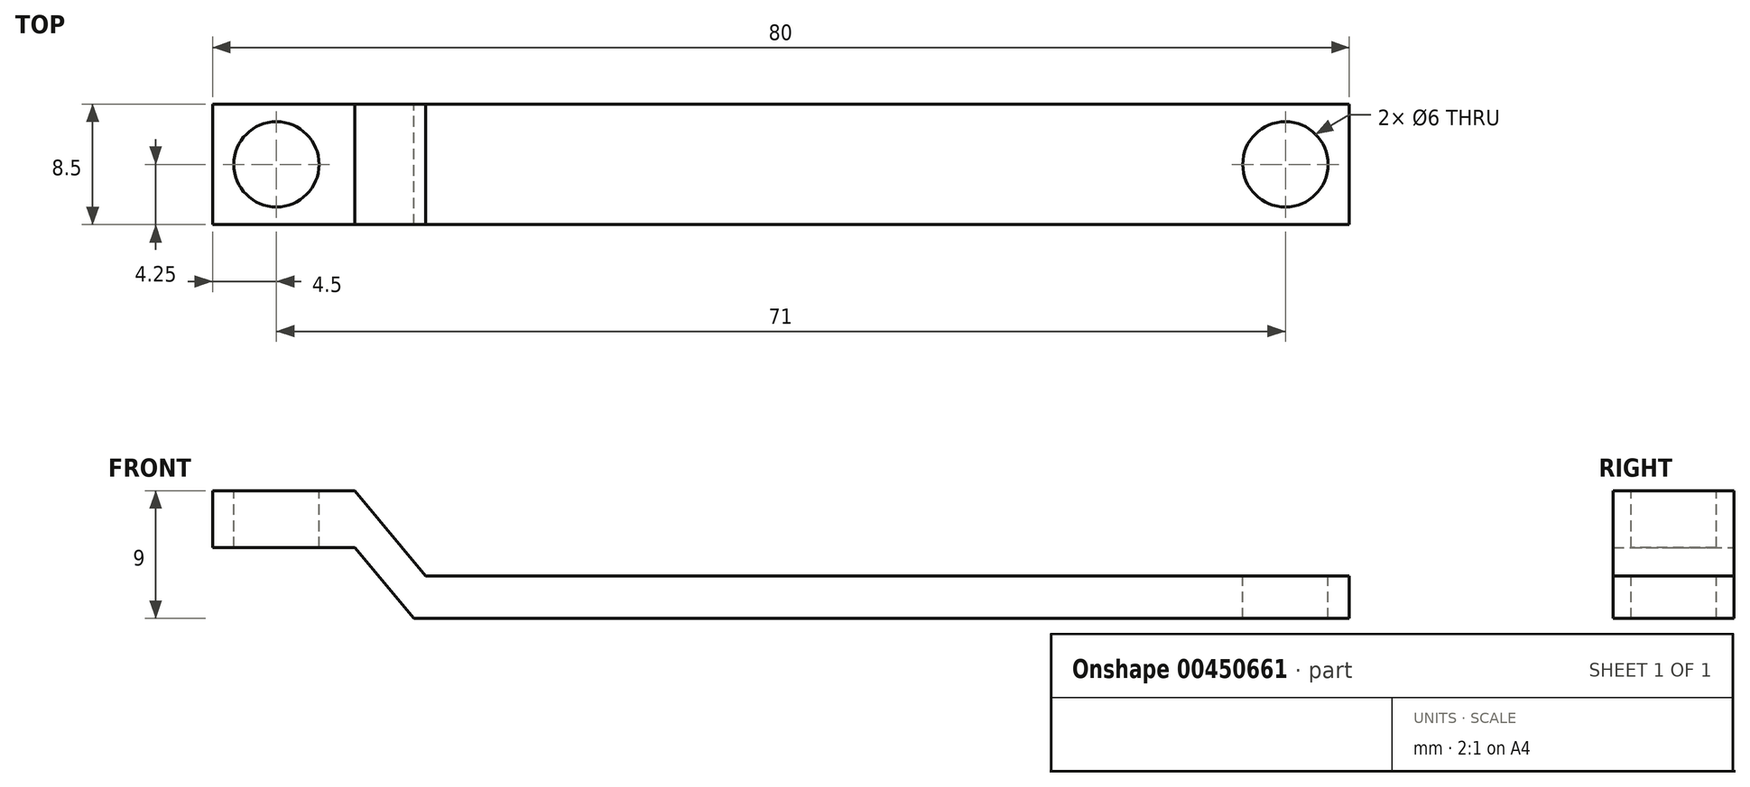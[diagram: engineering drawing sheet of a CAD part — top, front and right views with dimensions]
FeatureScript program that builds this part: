
annotation { "Feature Type Name" : "Feature", "Feature Type Description" : "" }
export const myFeature = defineFeature(function(context is Context, id is Id, definition is map)
    precondition{}
    {
        {
            var Q0;
            Q0=qCreatedBy(makeId("Front.planeOp"),FACE);
            var sketch = newSketch(context, id + "F0", { "sketchPlane" : qUnion([Q0])});
            skLineSegment(sketch, "E0.bottom", {"start": v(0, 0) * mm, "end": v(40, 0) * mm});
            skLineSegment(sketch, "E0.top", {"start": v(-25, 3) * mm, "end": v(40, 3) * mm});
            skLineSegment(sketch, "E0.right", {"start": v(40, 0) * mm, "end": v(40, 3) * mm});
            skLineSegment(sketch, "E1", {"start": v(-25, 3) * mm, "end": v(-30, 9) * mm});
            skLineSegment(sketch, "E2", {"start": v(-30, 9) * mm, "end": v(-40, 9) * mm});
            skLineSegment(sketch, "E3", {"start": v(-40, 9) * mm, "end": v(-40, 5) * mm});
            skLineSegment(sketch, "E4", {"start": v(-40, 5) * mm, "end": v(-30, 5) * mm});
            skLineSegment(sketch, "E5", {"start": v(-30, 5) * mm, "end": v(-25.83, 0) * mm});
            skLineSegment(sketch, "E6", {"start": v(-25.83, 0) * mm, "end": v(0, 0) * mm});
            skSolve(sketch);
        }
        {
            var Q0;
            Q0 = qSketchRegion(id + "F0", true);
            extrude(context, id + "F1", {"entities" : qUnion([Q0]), "endBound" : BoundingType.SYMMETRIC, "depth" : 8.5 * mm});
        }
        {
            var Q0;
            Q0=makeQuery(id+"F1.opExtrude","SWEPT_FACE",FACE,{"disambiguationData":[OSD([sQuery(id+"F0.wireOp",EDGE,"E2")])]});
            var sketch = newSketch(context, id + "F2", { "sketchPlane" : qUnion([Q0])});
            skCircle(sketch, "E7", {"center": v(-35.5, 0) * mm, "radius": 3 * mm});
            skCircle(sketch, "E8", {"center": v(35.5, 0) * mm, "radius": 3 * mm});
            skSolve(sketch);
        }
        {
            var Q0;
            Q0 = qSketchRegion(id + "F2", true);
            extrude(context, id + "F3", {"entities" : qUnion([Q0]), "operationType" : NewBodyOperationType.REMOVE, "oppositeDirection" : true, "depth" : 25 * mm});
        }
    });
